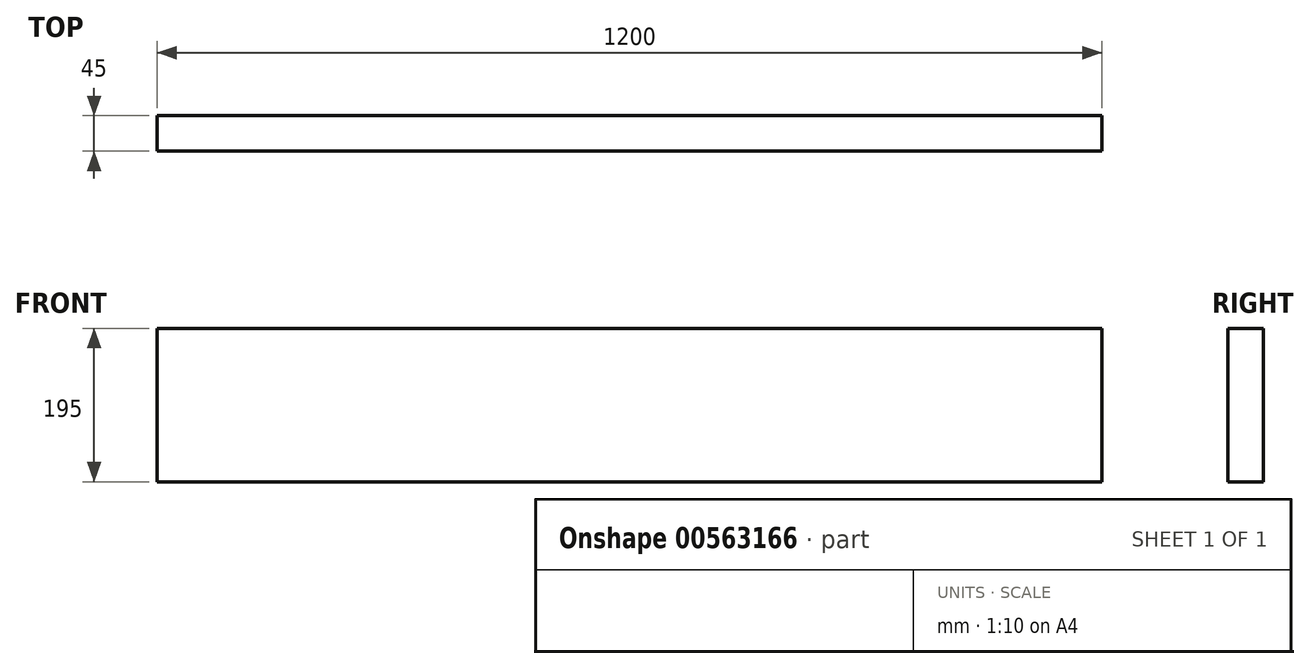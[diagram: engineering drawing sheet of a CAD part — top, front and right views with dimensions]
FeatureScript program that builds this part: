
annotation { "Feature Type Name" : "Feature", "Feature Type Description" : "" }
export const myFeature = defineFeature(function(context is Context, id is Id, definition is map)
    precondition{}
    {
        {
            var Q0;
            Q0=qCreatedBy(makeId("Front.planeOp"),FACE);
            var sketch = newSketch(context, id + "F0", { "sketchPlane" : qUnion([Q0])});
            skLineSegment(sketch, "E0.bottom", {"start": v(-1976.18, -361.1) * mm, "end": v(-776.18, -361.1) * mm});
            skLineSegment(sketch, "E0.top", {"start": v(-1976.18, -556.1) * mm, "end": v(-776.18, -556.1) * mm});
            skLineSegment(sketch, "E0.left", {"start": v(-1976.18, -361.1) * mm, "end": v(-1976.18, -556.1) * mm});
            skLineSegment(sketch, "E0.right", {"start": v(-776.18, -361.1) * mm, "end": v(-776.18, -556.1) * mm});
            skSolve(sketch);
        }
        {
            var Q0;
            Q0=makeQuery(id+"F0.imprint","IMPRINT",FACE,{"disambiguationData":[TD([[makeQuery(id+"F0.imprint","IMPRINT",EDGE,{"derivedFrom":sQuery(id+"F0.wireOp",EDGE,"E0.bottom")}),-1.0]])]});
            extrude(context, id + "F1", {"entities" : qUnion([Q0]), "depth" : 45 * mm, "offsetDistance" : 25 * mm});
        }
    });
